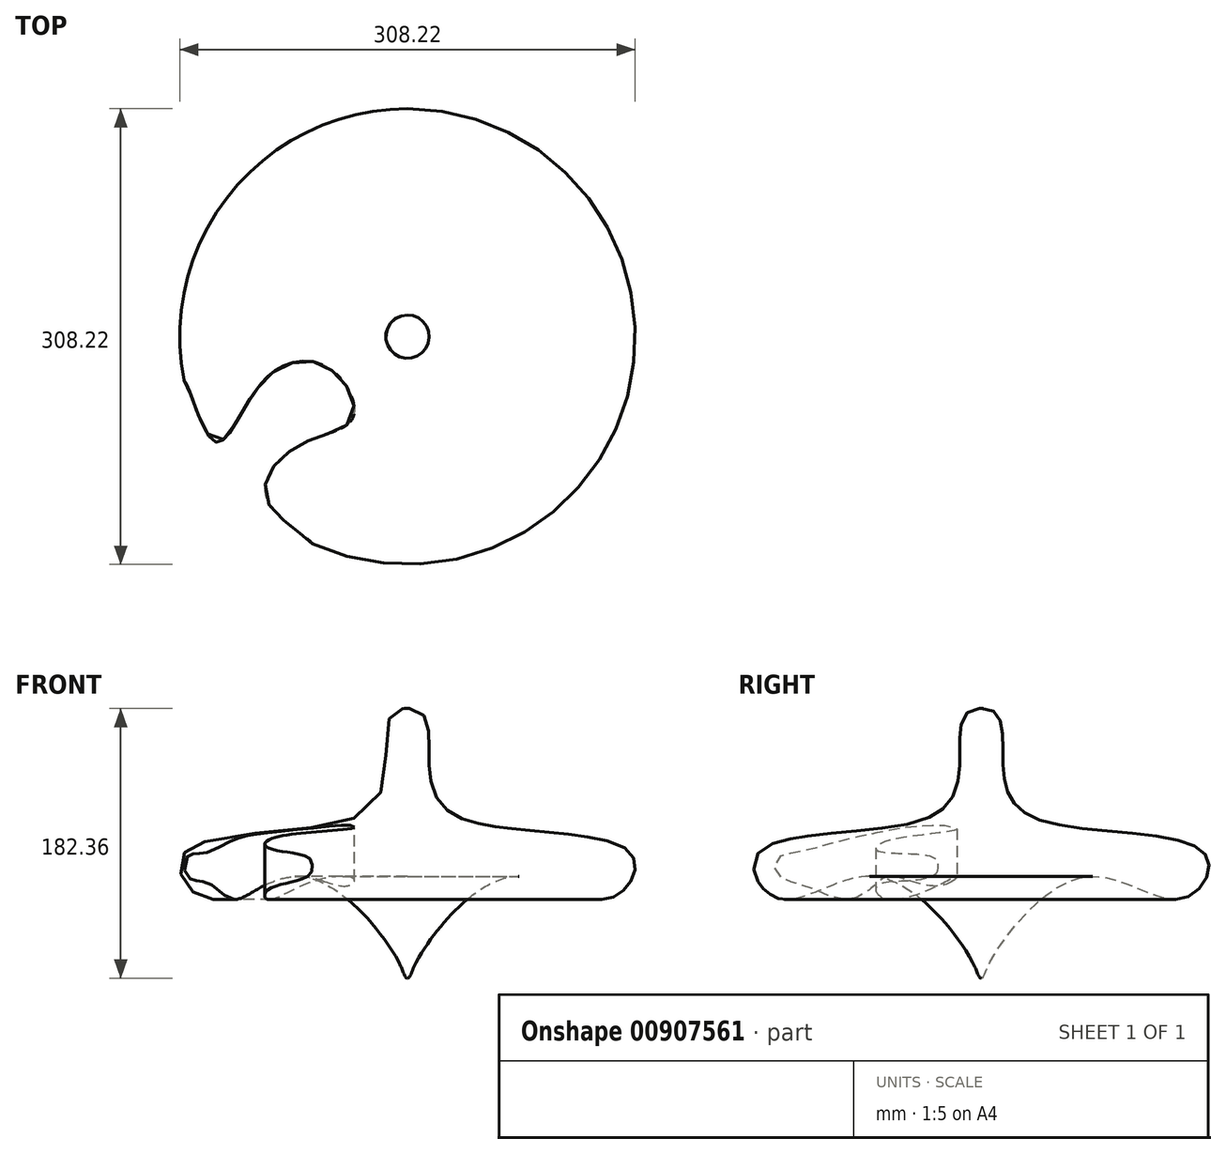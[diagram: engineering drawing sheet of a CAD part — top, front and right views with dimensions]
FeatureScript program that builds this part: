
annotation { "Feature Type Name" : "Feature", "Feature Type Description" : "" }
export const myFeature = defineFeature(function(context is Context, id is Id, definition is map)
    precondition{}
    {
        {
            var Q0;
            Q0=qCreatedBy(makeId("Right.planeOp"),FACE);
            var sketch = newSketch(context, id + "F0", { "sketchPlane" : qUnion([Q0])});
            skFitSpline(sketch, "E0", {"points": [v(0, 0) * mm, v(4.96, 8.86) * mm, v(69.96, 68.48) * mm, v(136.67, 53.75) * mm, v(151.72, 83.66) * mm, v(36.8, 107.91) * mm, v(14.62, 148.36) * mm, v(0, 182.32) * mm], "startDerivative": vector(88.3, 0) * mm, "endDerivative": vector(-415.55, -23.3) * mm});
            skLineSegment(sketch, "E1", {"start": v(0, 182.32) * mm, "end": v(0, 0) * mm});
            skSolve(sketch);
        }
        {
            var Q0;
            Q0=makeQuery(id+"F0.imprint","IMPRINT",FACE,{"disambiguationData":[TD([[makeQuery(id+"F0.imprint","IMPRINT",EDGE,{"derivedFrom":sQuery(id+"F0.wireOp",EDGE,"E0")}),1.0]])]});
            var Q1;
            Q1=sQuery(id+"F0.wireOp",EDGE,"E1");
            revolve(context, id + "F1", {"surfaceOperationType" : NewSurfaceOperationType.NEW, "entities" : qUnion([Q0]), "axis" : qUnion([Q1]), "revolveType" : RevolveType.FULL});
        }
        {
            var Q0;
            Q0=qCreatedBy(makeId("Top.planeOp"),FACE);
            var sketch = newSketch(context, id + "F2", { "sketchPlane" : qUnion([Q0])});
            skFitSpline(sketch, "E2", {"points": [v(-64.16, -140.49) * mm, v(-95.21, -110.46) * mm, v(-72.3, -72.94) * mm, v(-36.9, -54.74) * mm, v(-53.31, -21.24) * mm, v(-97.79, -30.29) * mm, v(-130.45, -71.04) * mm, v(-150.8, -29.8) * mm, v(-124.4, -105.6) * mm, v(-64.16, -140.49) * mm]});
            skSolve(sketch);
        }
        {
            var Q0;
            Q0=makeQuery(id+"F2.imprint","IMPRINT",FACE,{"disambiguationData":[TD([[makeQuery(id+"F2.imprint","IMPRINT",EDGE,{"derivedFrom":sQuery(id+"F2.wireOp",EDGE,"E2")}),1.0]])]});
            extrude(context, id + "F3", {"entities" : qUnion([Q0]), "operationType" : NewBodyOperationType.REMOVE, "depth" : 148.2 * mm, "offsetDistance" : 25 * mm});
        }
    });
